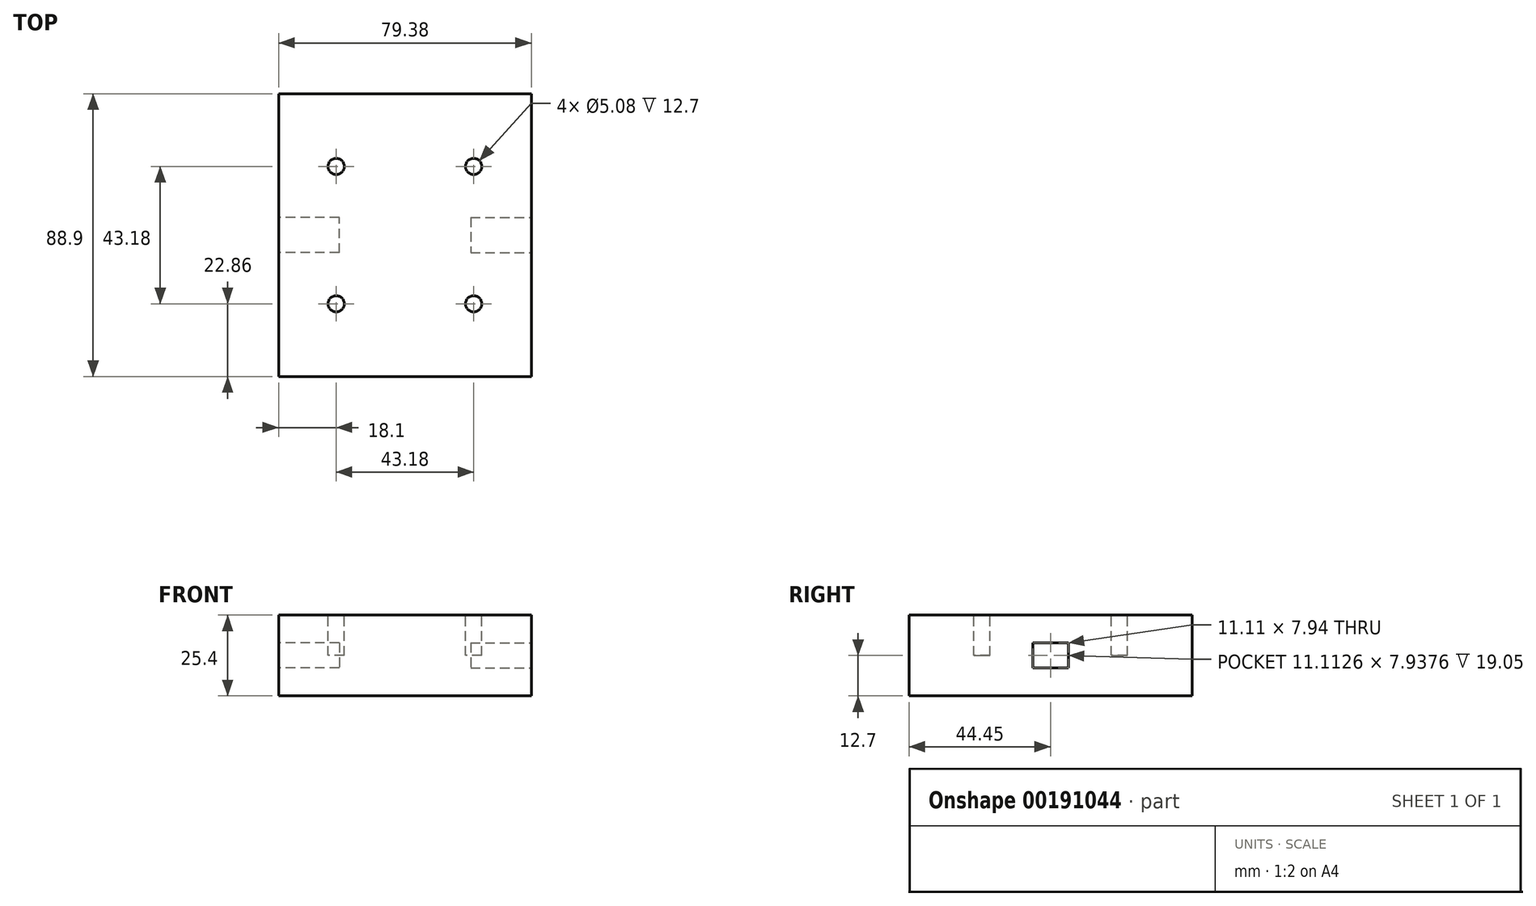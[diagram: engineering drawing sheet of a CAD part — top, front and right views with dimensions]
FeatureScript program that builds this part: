
annotation { "Feature Type Name" : "Feature", "Feature Type Description" : "" }
export const myFeature = defineFeature(function(context is Context, id is Id, definition is map)
    precondition{}
    {
        {
            var Q0;
            Q0=qCreatedBy(makeId("Front.planeOp"),FACE);
            var sketch = newSketch(context, id + "F0", { "sketchPlane" : qUnion([Q0])});
            skLineSegment(sketch, "E0.bottom", {"start": v(39.69, 12.7) * mm, "end": v(-39.69, 12.7) * mm});
            skLineSegment(sketch, "E0.top", {"start": v(39.69, -12.7) * mm, "end": v(-39.69, -12.7) * mm});
            skLineSegment(sketch, "E0.left", {"start": v(39.69, 12.7) * mm, "end": v(39.69, -12.7) * mm});
            skLineSegment(sketch, "E0.right", {"start": v(-39.69, 12.7) * mm, "end": v(-39.69, -12.7) * mm});
            skPoint(sketch, "E0.middle", {"position": v(0, 0) * mm});
            skSolve(sketch);
        }
        {
            var Q0;
            Q0 = qSketchRegion(id + "F0", true);
            extrude(context, id + "F1", {"entities" : qUnion([Q0]), "depth" : 88.9 * mm});
        }
        {
            var Q0;
            Q0=makeQuery(id+"F1.opExtrude","SWEPT_FACE",FACE,{"disambiguationData":[OSD([sQuery(id+"F0.wireOp",EDGE,"E0.left")])]});
            var sketch = newSketch(context, id + "F2", { "sketchPlane" : qUnion([Q0])});
            skLineSegment(sketch, "E1", {"start": v(0, 0) * mm, "end": v(-88.9, 0) * mm});
            skPoint(sketch, "E2", {"position": v(-44.45, 0) * mm});
            skLineSegment(sketch, "E3.bottom", {"start": v(-38.9, 3.97) * mm, "end": v(-50, 3.97) * mm});
            skLineSegment(sketch, "E3.top", {"start": v(-38.9, -3.97) * mm, "end": v(-50, -3.97) * mm});
            skLineSegment(sketch, "E3.left", {"start": v(-38.9, 3.97) * mm, "end": v(-38.9, -3.97) * mm});
            skLineSegment(sketch, "E3.right", {"start": v(-50, 3.97) * mm, "end": v(-50, -3.97) * mm});
            skSolve(sketch);
        }
        {
            var Q0;
            Q0 = qSketchRegion(id + "F2", true);
            extrude(context, id + "F3", {"entities" : qUnion([Q0]), "operationType" : NewBodyOperationType.REMOVE, "oppositeDirection" : true, "depth" : 19.05 * mm});
        }
        {
            var Q0;
            Q0=makeQuery(id+"F1.opExtrude","SWEPT_FACE",FACE,{"disambiguationData":[OSD([sQuery(id+"F0.wireOp",EDGE,"E0.right")])]});
            var sketch = newSketch(context, id + "F4", { "sketchPlane" : qUnion([Q0])});
            skLineSegment(sketch, "E4", {"start": v(0, 0) * mm, "end": v(88.9, 0) * mm});
            skPoint(sketch, "E5", {"position": v(44.45, 0) * mm});
            skLineSegment(sketch, "E6.bottom", {"start": v(50, 3.97) * mm, "end": v(38.9, 3.97) * mm});
            skLineSegment(sketch, "E6.top", {"start": v(50, -3.97) * mm, "end": v(38.9, -3.97) * mm});
            skLineSegment(sketch, "E6.left", {"start": v(50, 3.97) * mm, "end": v(50, -3.97) * mm});
            skLineSegment(sketch, "E6.right", {"start": v(38.9, 3.97) * mm, "end": v(38.9, -3.97) * mm});
            skSolve(sketch);
        }
        {
            var Q0;
            Q0 = qSketchRegion(id + "F4", true);
            extrude(context, id + "F5", {"entities" : qUnion([Q0]), "operationType" : NewBodyOperationType.REMOVE, "oppositeDirection" : true, "depth" : 19.05 * mm});
        }
        {
            var Q0;
            Q0=makeQuery(id+"F1.opExtrude","SWEPT_FACE",FACE,{"disambiguationData":[OSD([sQuery(id+"F0.wireOp",EDGE,"E0.bottom")])]});
            var sketch = newSketch(context, id + "F6", { "sketchPlane" : qUnion([Q0])});
            skLineSegment(sketch, "E7", {"start": v(0, 0) * mm, "end": v(0, -88.9) * mm});
            skPoint(sketch, "E8", {"position": v(0, -44.45) * mm});
            skPoint(sketch, "E9", {"position": v(0, -66.04) * mm});
            skPoint(sketch, "E10", {"position": v(0, -22.86) * mm});
            skPoint(sketch, "E11", {"position": v(21.6, -66.04) * mm});
            skPoint(sketch, "E12", {"position": v(-21.59, -66.04) * mm});
            skPoint(sketch, "E13", {"position": v(21.59, -22.86) * mm});
            skPoint(sketch, "E14", {"position": v(-21.59, -22.86) * mm});
            skCircle(sketch, "E15", {"center": v(-21.59, -22.86) * mm, "radius": 2.54 * mm});
            skCircle(sketch, "E16", {"center": v(21.59, -22.86) * mm, "radius": 2.54 * mm});
            skCircle(sketch, "E17", {"center": v(21.6, -66.04) * mm, "radius": 2.54 * mm});
            skCircle(sketch, "E18", {"center": v(-21.59, -66.04) * mm, "radius": 2.54 * mm});
            skSolve(sketch);
        }
        {
            var Q0;
            Q0 = qSketchRegion(id + "F6", true);
            extrude(context, id + "F7", {"entities" : qUnion([Q0]), "operationType" : NewBodyOperationType.REMOVE, "oppositeDirection" : true, "depth" : 12.7 * mm});
        }
    });
